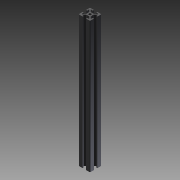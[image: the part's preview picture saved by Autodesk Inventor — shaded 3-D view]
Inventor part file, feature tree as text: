
AUTODESK INVENTOR PART (.ipt)
format: ipt  version: 2016 (Build 200138000, 138)  size: 196,096 bytes
history: native  units: mm
features: other x7, sketch x2, extrude x1, hole x1
ambient origin geometry x8: Origin, YZ Plane, XZ Plane, XY Plane, X Axis, Y Axis, Z Axis, Center Point
bodies: Solid1 (feature_tree)
feature tree (11):
  extrude  "Extrusion1"  TaperAngle=0.0deg  [1 undecoded]
  hole  "Hole1"  [1 undecoded]
  other  "C1_XY"
  other  "C1_YZ"
  other  "C1_ZX"
  other  "C1_X"
  other  "C1_Y"
  other  "C1_Z"
  other  "C1_Center"
  sketch  "Sketch_75"  dims[d2=4.2mm d3=6.0mm d4=4.0mm d5=2.0mm d6=90.0deg d7=230.0mm d8=0.0mm d9=0.0mm]
  sketch  "Sketch2"  dims[d0=230.0mm d1=0.0mm]
note: 2 required parameter values undecoded (feature->parameter linkage not recoverable at this tier; creation-order binding heuristic only, values carry confidence <= 0.55)
